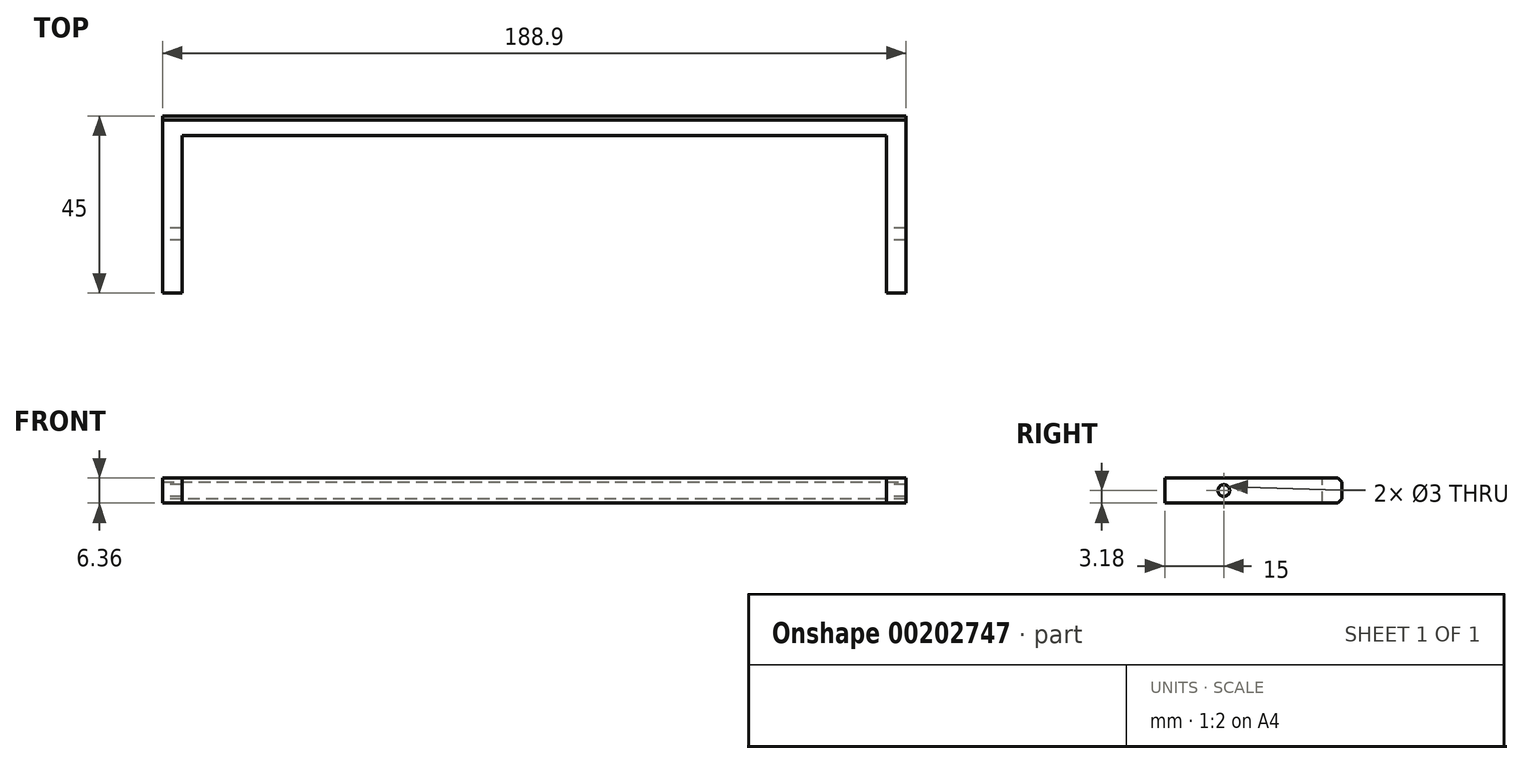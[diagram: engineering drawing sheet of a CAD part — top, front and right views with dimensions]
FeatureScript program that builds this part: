
annotation { "Feature Type Name" : "Feature", "Feature Type Description" : "" }
export const myFeature = defineFeature(function(context is Context, id is Id, definition is map)
    precondition{}
    {
        {
            var Q0;
            Q0=qCreatedBy(makeId("Top.planeOp"),FACE);
            var sketch = newSketch(context, id + "F0", { "sketchPlane" : qUnion([Q0])});
            skLineSegment(sketch, "E0.top", {"start": v(94.45, 22.5) * mm, "end": v(-94.45, 22.5) * mm});
            skLineSegment(sketch, "E0.left", {"start": v(94.45, -22.5) * mm, "end": v(94.45, 22.5) * mm});
            skLineSegment(sketch, "E0.right", {"start": v(-94.45, -22.5) * mm, "end": v(-94.45, 22.5) * mm});
            skPoint(sketch, "E0.middle", {"position": v(0, 0) * mm});
            skLineSegment(sketch, "E1.left", {"start": v(89.45, -15.17) * mm, "end": v(89.45, 15.17) * mm});
            skLineSegment(sketch, "E1.right", {"start": v(-89.45, -15.17) * mm, "end": v(-89.45, 15.17) * mm});
            skLineSegment(sketch, "E2", {"start": v(-94.45, -22.5) * mm, "end": v(-89.45, -22.5) * mm});
            skLineSegment(sketch, "E3", {"start": v(-89.45, -22.5) * mm, "end": v(-89.45, -15.17) * mm});
            skLineSegment(sketch, "E4", {"start": v(89.45, -15.17) * mm, "end": v(89.45, -22.5) * mm});
            skLineSegment(sketch, "E5", {"start": v(89.45, -22.5) * mm, "end": v(94.45, -22.5) * mm});
            skLineSegment(sketch, "E6", {"start": v(-89.45, 17.5) * mm, "end": v(89.45, 17.5) * mm});
            skLineSegment(sketch, "E7", {"start": v(-89.45, 15.17) * mm, "end": v(-89.45, 17.5) * mm});
            skLineSegment(sketch, "E8", {"start": v(89.45, 15.17) * mm, "end": v(89.45, 17.5) * mm});
            skPoint(sketch, "E9.orphan", {"position": v(-94.45, 17.5) * mm});
            skSolve(sketch);
        }
        {
            var Q0;
            Q0 = qSketchRegion(id + "F0", true);
            extrude(context, id + "F1", {"entities" : qUnion([Q0]), "endBound" : BoundingType.SYMMETRIC, "oppositeDirection" : true, "depth" : 6.35 * mm});
        }
        {
            var Q0;
            Q0=makeQuery(id+"F1.opExtrude","SWEPT_FACE",FACE,{"disambiguationData":[OSD([sQuery(id+"F0.wireOp",EDGE,"E0.right")])]});
            var sketch = newSketch(context, id + "F2", { "sketchPlane" : qUnion([Q0])});
            skPoint(sketch, "E10", {"position": v(7.5, 0) * mm});
            skSolve(sketch);
        }
        {
            var Q0;
            Q0=sQuery(id+"F2.wireOp",VERTEX,"E10");
            var Q1;
            Q1=makeQuery(id+"F1.opExtrude","SWEPT_BODY",BODY,{"disambiguationData":[OSD([sQuery(id+"F0.wireOp",EDGE,"E0.top"),sQuery(id+"F0.wireOp",EDGE,"E0.left"),sQuery(id+"F0.wireOp",EDGE,"E0.right"),sQuery(id+"F0.wireOp",EDGE,"E1.left"),sQuery(id+"F0.wireOp",EDGE,"E1.right"),sQuery(id+"F0.wireOp",EDGE,"E2"),sQuery(id+"F0.wireOp",EDGE,"E3"),sQuery(id+"F0.wireOp",EDGE,"E4"),sQuery(id+"F0.wireOp",EDGE,"E5"),sQuery(id+"F0.wireOp",EDGE,"E6"),sQuery(id+"F0.wireOp",EDGE,"E7"),sQuery(id+"F0.wireOp",EDGE,"E8")])]});
            hole(context, id + "F3", {"style" : HoleStyle.SIMPLE, "endStyle" : HoleEndStyle.THROUGH, "standardTappedOrClearance" : lookupTablePath({ "standard" : "ISO", "size" : "3", "type" : "Drilled" }), "standardBlindInLast" : lookupTablePath({ "standard" : "ISO", "size" : "3", "type" : "Drilled" }), "holeDiameter" : 3 * mm, "startFromSketch" : true, "locations" : qUnion([Q0]), "scope" : qUnion([Q1]), "isTappedThrough" : true});
        }
        {
            var Q0;
            Q0=makeQuery(id+"F1.opExtrude","CAP_EDGE",EDGE,{"disambiguationData":[OSD([sQuery(id+"F0.wireOp",EDGE,"E0.top")])],"isStart":true});
            chamfer(context, id + "F4", {"entities" : qUnion([Q0]), "chamferType" : ChamferType.OFFSET_ANGLE, "width" : 1 * mm, "oppositeDirection" : false, "angle" : 45 * degree, "tangentPropagation" : true});
        }
        {
            var Q0;
            Q0=makeQuery(id+"F1.opExtrude","CAP_EDGE",EDGE,{"disambiguationData":[OSD([sQuery(id+"F0.wireOp",EDGE,"E0.top")])],"isStart":false});
            chamfer(context, id + "F5", {"entities" : qUnion([Q0]), "chamferType" : ChamferType.OFFSET_ANGLE, "width" : 1 * mm, "oppositeDirection" : false, "angle" : 45 * degree, "tangentPropagation" : true});
        }
    });
